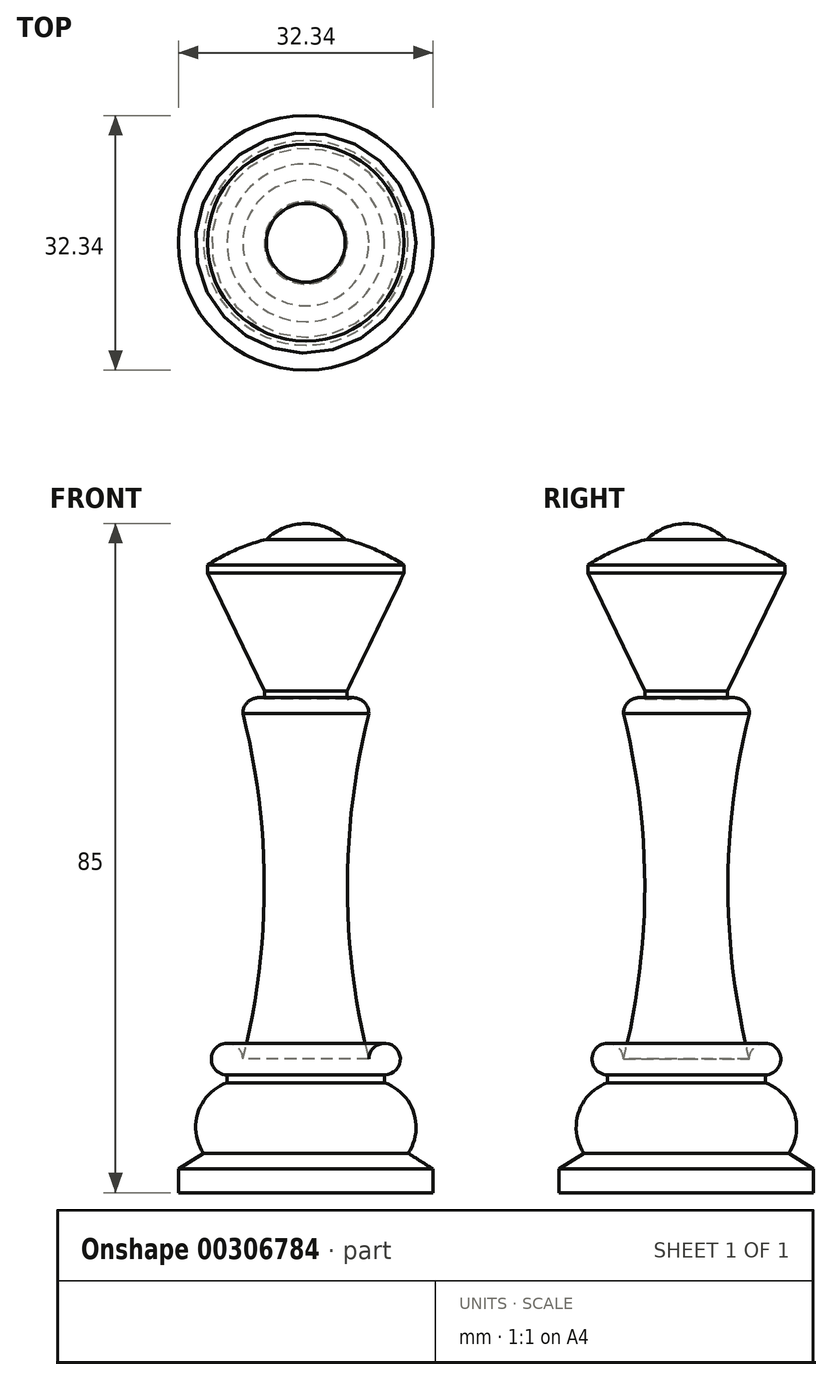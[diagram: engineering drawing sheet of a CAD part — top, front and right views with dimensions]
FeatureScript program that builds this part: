
annotation { "Feature Type Name" : "Feature", "Feature Type Description" : "" }
export const myFeature = defineFeature(function(context is Context, id is Id, definition is map)
    precondition{}
    {
        {
            var Q0;
            Q0=qCreatedBy(makeId("Front.planeOp"),FACE);
            var sketch = newSketch(context, id + "F0", { "sketchPlane" : qUnion([Q0])});
            skArc(sketch, "E0", {"start": v(5, -2) * mm, "mid": v(2.7, -0.52) * mm, "end": v(0, 0) * mm});
            skArc(sketch, "E1", {"start": v(12.5, -5.27) * mm, "mid": v(8.88, -3.33) * mm, "end": v(5, -2) * mm});
            skLineSegment(sketch, "E2", {"start": v(12.5, -5.27) * mm, "end": v(12.5, -6.27) * mm});
            skLineSegment(sketch, "E3", {"start": v(12.5, -6.27) * mm, "end": v(5.24, -21.27) * mm});
            skLineSegment(sketch, "E4", {"start": v(5.24, -21.27) * mm, "end": v(5.24, -22.27) * mm});
            skArc(sketch, "E5", {"start": v(8, -24.12) * mm, "mid": v(7.12, -22.46) * mm, "end": v(5.24, -22.27) * mm});
            skArc(sketch, "E6", {"start": v(8, -24.12) * mm, "mid": v(5.28, -46.08) * mm, "end": v(8, -68.03) * mm});
            skArc(sketch, "E7", {"start": v(10, -70.03) * mm, "mid": v(11.41, -66.61) * mm, "end": v(8, -68.03) * mm});
            skLineSegment(sketch, "E8", {"start": v(10, -70.03) * mm, "end": v(10, -71.03) * mm});
            skArc(sketch, "E9", {"start": v(13, -80) * mm, "mid": v(13.7, -74.79) * mm, "end": v(10, -71.03) * mm});
            skLineSegment(sketch, "E10", {"start": v(13, -80) * mm, "end": v(16.17, -82) * mm});
            skLineSegment(sketch, "E11", {"start": v(16.17, -82) * mm, "end": v(16.17, -85) * mm});
            skLineSegment(sketch, "E12", {"start": v(16.17, -85) * mm, "end": v(0, -85) * mm});
            skLineSegment(sketch, "E13", {"start": v(0, 0) * mm, "end": v(0, -85) * mm});
            skSolve(sketch);
        }
        {
            var Q0;
            Q0=makeQuery(id+"F0.imprint","IMPRINT",FACE,{"disambiguationData":[TD([[makeQuery(id+"F0.imprint","IMPRINT",EDGE,{"derivedFrom":sQuery(id+"F0.wireOp",EDGE,"E0")}),1.0]])]});
            var Q1;
            Q1=sQuery(id+"F0.wireOp",EDGE,"E13");
            revolve(context, id + "F1", {"entities" : qUnion([Q0]), "axis" : qUnion([Q1]), "revolveType" : RevolveType.FULL});
        }
    });
